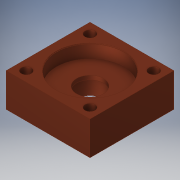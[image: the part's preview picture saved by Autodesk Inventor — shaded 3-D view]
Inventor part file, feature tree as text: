
AUTODESK INVENTOR PART (.ipt)
format: ipt  version: 2018 (Build 220112000, 112)  size: 153,088 bytes
history: native  units: in
note: dims shown in document units (in); Inventor stores cm internally (conversion verified against a paired STEP export)
features: sketch x6, extrude x5, hole x1
ambient origin geometry x8: Origin, YZ Plane, XZ Plane, XY Plane, X Axis, Y Axis, Z Axis, Center Point
bodies: Solid1 (feature_tree)
feature tree (12):
  extrude  "Extrusion1"  Depth=1.25in
  extrude  "Extrusion2"  Depth=0.5in TaperAngle=0.0deg
  hole  "Hole1"  [1 undecoded]
  extrude  "Extrusion3"  Depth=0.15in
  extrude  "Extrusion4"  Depth=0.25in
  extrude  "Extrusion5"  Depth=0.24in
  sketch  "Sketch1"  dims[d0=0.4in d1=1.25in]
  sketch  "Sketch2"  dims[d2=1.25in d3=0.5in d4=0.0in]
  sketch  "Sketch3"  dims[d5=1.0in d6=0.2in d7=0.0in]
  sketch  "Sketch4"  dims[d8=0.15in d9=0.15in]
  sketch  "Sketch5"  dims[d10=0.15in d11=0.75in d12=0.279in d13=0.25in d14=0.5635in d15=1.0in d16=0.8108in d17=1.01in]
  sketch  "Sketch6"  dims[d18=0.01in d19=0.0in d20=0.51in d21=0.002in d22=0.0in d23=0.5in d24=0.24in d25=0.0in]
note: 1 required parameter value undecoded (feature->parameter linkage not recoverable at this tier; creation-order binding heuristic only, values carry confidence <= 0.55)
